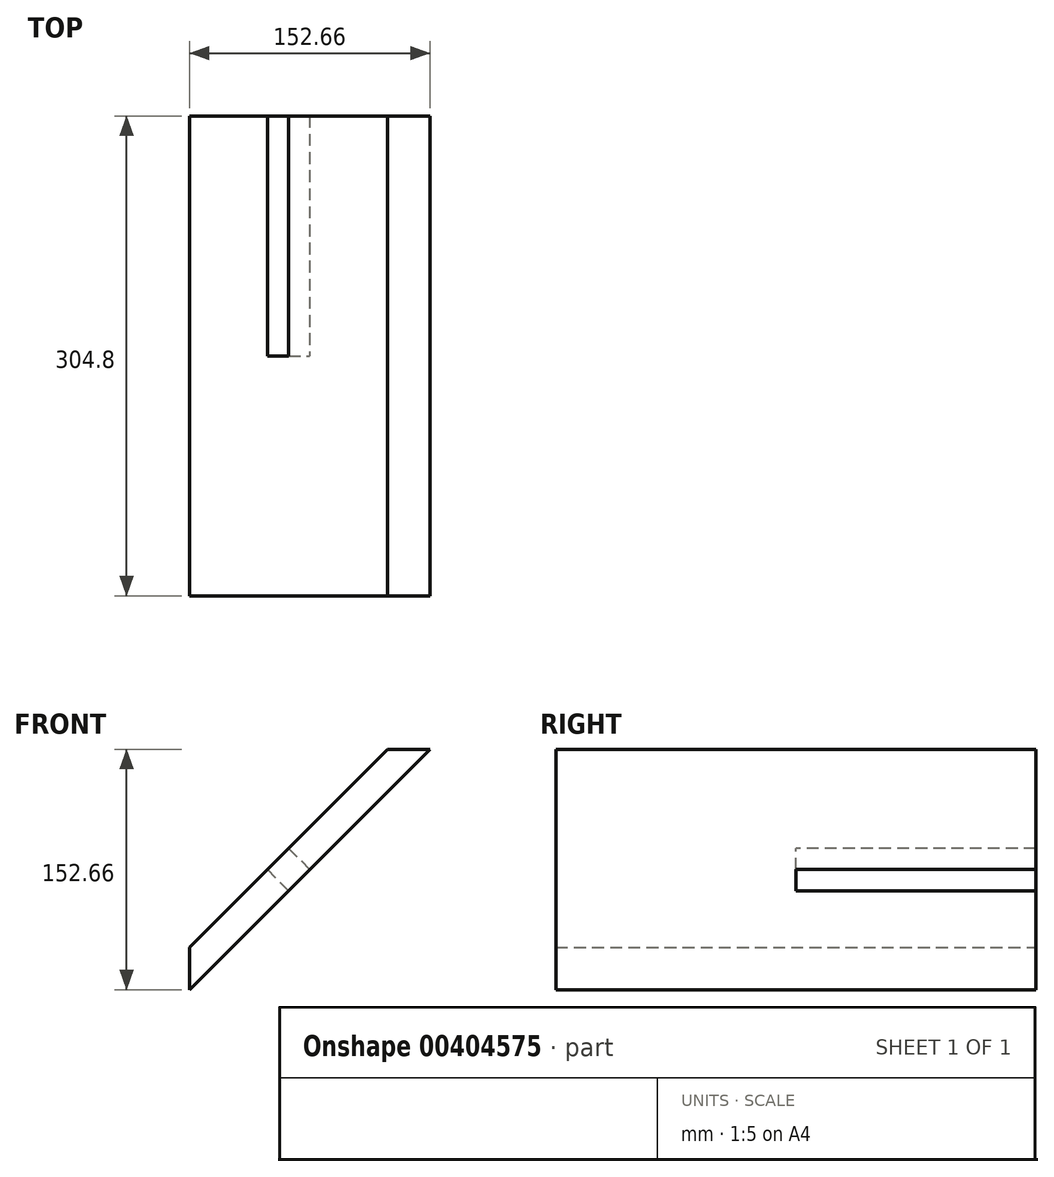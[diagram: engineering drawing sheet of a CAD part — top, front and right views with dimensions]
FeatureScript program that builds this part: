
annotation { "Feature Type Name" : "Feature", "Feature Type Description" : "" }
export const myFeature = defineFeature(function(context is Context, id is Id, definition is map)
    precondition{}
    {
        {
            var Q0;
            Q0=qCreatedBy(makeId("Front.planeOp"),FACE);
            var sketch = newSketch(context, id + "F0", { "sketchPlane" : qUnion([Q0])});
            skLineSegment(sketch, "E0.left", {"start": v(-421.52, 0) * mm, "end": v(-421.52, 26.94) * mm});
            skPoint(sketch, "E0.middle", {"position": v(22.97, 488.94) * mm});
            skLineSegment(sketch, "E1", {"start": v(-421.52, 0) * mm, "end": v(-268.86, 152.66) * mm});
            skLineSegment(sketch, "E2", {"start": v(-421.52, 26.94) * mm, "end": v(-295.8, 152.66) * mm});
            skLineSegment(sketch, "E3", {"start": v(-268.86, 152.66) * mm, "end": v(-295.8, 152.66) * mm});
            skSolve(sketch);
        }
        {
            var Q0;
            Q0=qSketchRegion(id+"F0",true);
            extrude(context, id + "F1", {"entities" : qUnion([Q0]), "endBound" : BoundingType.SYMMETRIC, "depth" : 304.8 * mm});
        }
        {
            var Q0;
            Q0=makeQuery(id+"F1.opExtrude","SWEPT_FACE",FACE,{"disambiguationData":[OSD([sQuery(id+"F0.wireOp",EDGE,"E2")])]});
            var sketch = newSketch(context, id + "F2", { "sketchPlane" : qUnion([Q0])});
            skLineSegment(sketch, "E4.bottom", {"start": v(-152.4, -209.16) * mm, "end": v(0, -209.16) * mm});
            skLineSegment(sketch, "E4.top", {"start": v(-152.4, -190.11) * mm, "end": v(0, -190.11) * mm});
            skLineSegment(sketch, "E4.left", {"start": v(-152.4, -209.16) * mm, "end": v(-152.4, -190.11) * mm});
            skLineSegment(sketch, "E4.right", {"start": v(0, -209.16) * mm, "end": v(0, -190.11) * mm});
            skSolve(sketch);
        }
        {
            var Q0;
            Q0=qSketchRegion(id+"F2",true);
            extrude(context, id + "F3", {"entities" : qUnion([Q0]), "operationType" : NewBodyOperationType.REMOVE, "oppositeDirection" : true, "depth" : 19.05 * mm});
        }
    });
